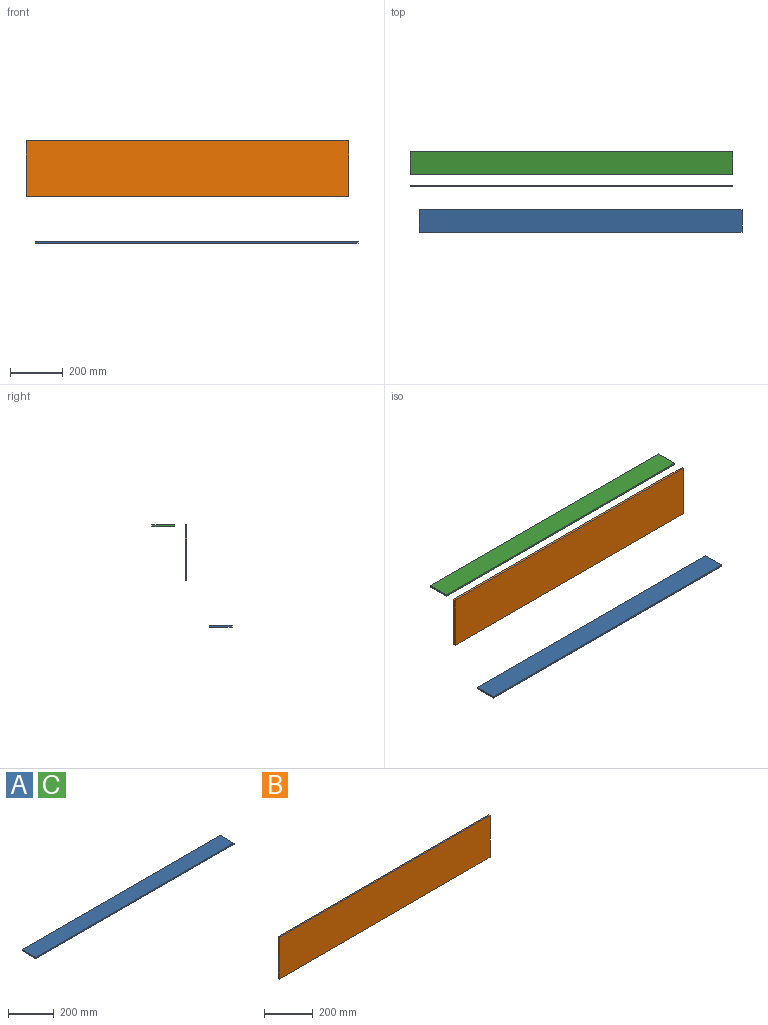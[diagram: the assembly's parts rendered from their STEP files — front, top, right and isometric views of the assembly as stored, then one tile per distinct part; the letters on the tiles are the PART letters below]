
ASSEMBLY  parts=3 mates=2
PART A: 6 faces, bbox 1219.2x85.7x6.4 mm
  f0: plane 1219.2x6.35mm, normal (0,1,0), area 7741.9mm2, adj f1,f3,f4,f5
  f1: plane 85.73x6.35mm, normal (-1,0,0), area 544.4mm2, adj f0,f2,f4,f5
  f2: plane 1219.2x6.35mm, normal (0,-1,0), area 7741.9mm2, adj f1,f3,f4,f5
  f3: plane 85.73x6.35mm, normal (1,0,0), area 544.4mm2, adj f0,f2,f4,f5
  f4: plane 1219.2x85.73mm, normal (0,0,1), area 104515.9mm2, adj f0,f1,f2,f3
  f5: plane 1219.2x85.73mm, normal (0,0,-1), area 104515.9mm2, adj f0,f1,f2,f3
PART B: 6 faces, bbox 1219.2x6.4x209.6 mm
  f0: plane 1219.2x6.35mm, normal (0,0,1), area 7741.9mm2, adj f1,f3,f4,f5
  f1: plane 209.55x6.35mm, normal (-1,0,0), area 1330.6mm2, adj f0,f2,f4,f5
  f2: plane 1219.2x6.35mm, normal (0,0,-1), area 7741.9mm2, adj f1,f3,f4,f5
  f3: plane 209.55x6.35mm, normal (1,0,0), area 1330.6mm2, adj f0,f2,f4,f5
  f4: plane 1219.2x209.55mm, normal (0,-1,0), area 255483.4mm2, adj f0,f1,f2,f3
  f5: plane 1219.2x209.55mm, normal (0,1,0), area 255483.4mm2, adj f0,f1,f2,f3
PART C: same geometry as A
PLACE A t=(41.1,-135.71,-322.89)mm
PLACE B t=(5.98,41.53,63.32)mm
PLACE C t=(5.98,81.75,56.97)mm
MATE planar B.f3 <-> C.f3  axis (1,0,0) through (615.58,41.53,63.32)mm
MATE planar C.f4 <-> B.f0  axis (0,0,1) through (615.58,81.75,63.32)mm
